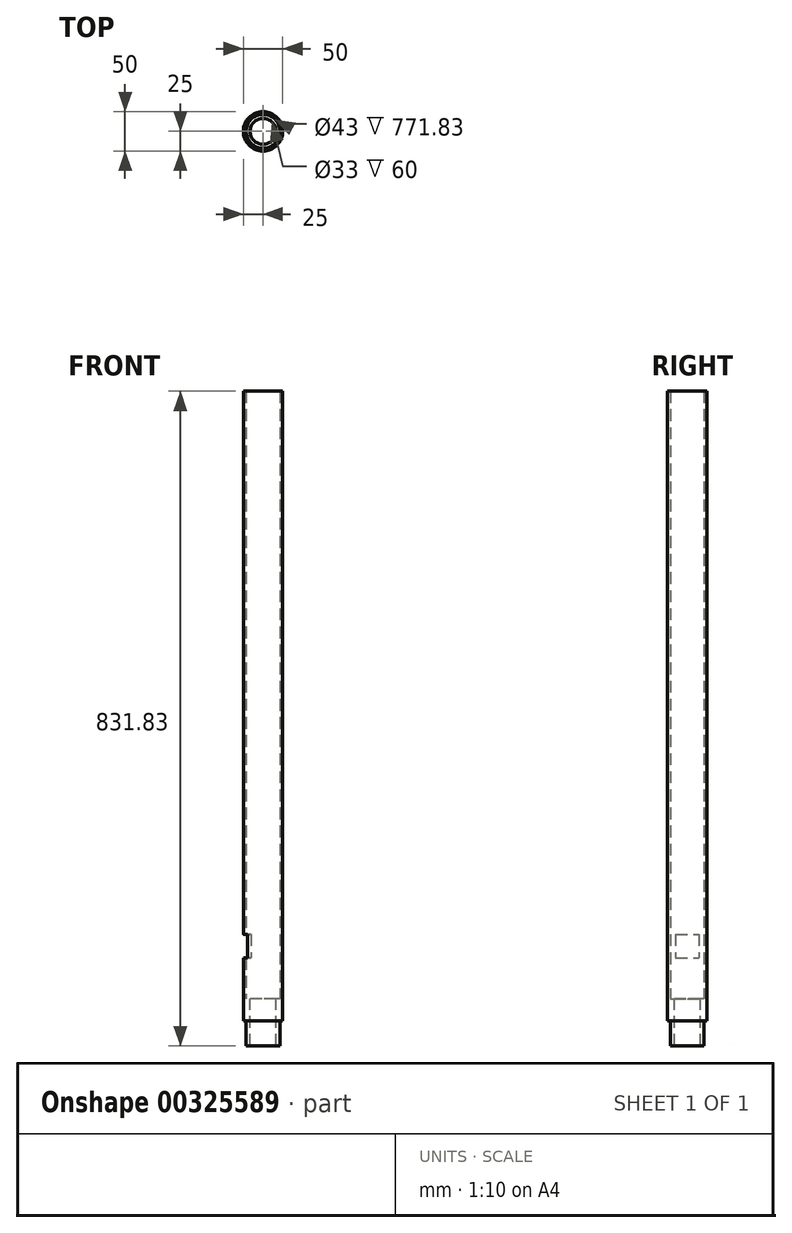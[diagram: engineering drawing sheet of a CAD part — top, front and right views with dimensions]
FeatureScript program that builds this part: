
annotation { "Feature Type Name" : "Feature", "Feature Type Description" : "" }
export const myFeature = defineFeature(function(context is Context, id is Id, definition is map)
    precondition{}
    {
        {
            var Q0;
            Q0=qCreatedBy(makeId("Top.planeOp"),FACE);
            var sketch = newSketch(context, id + "F0", { "sketchPlane" : qUnion([Q0])});
            skCircle(sketch, "E0", {"center": v(0, 0) * mm, "radius": 25 * mm});
            skCircle(sketch, "E1", {"center": v(0, 0) * mm, "radius": 21.5 * mm});
            skSolve(sketch);
        }
        {
            var Q0;
            Q0=makeQuery(id+"F0.imprint","IMPRINT",FACE,{"disambiguationData":[TD([[makeQuery(id+"F0.imprint","IMPRINT",EDGE,{"derivedFrom":sQuery(id+"F0.wireOp",EDGE,"E0")}),1.0]])]});
            extrude(context, id + "F1", {"entities" : qUnion([Q0]), "depth" : 800 * mm});
        }
        {
            var Q0;
            Q0 = qSketchRegion(id + "F0", true);
            extrude(context, id + "F2", {"entities" : qUnion([Q0]), "depth" : 200 * mm});
        }
        {
            var Q0;
            Q0=qCreatedBy(makeId("Right.planeOp"),FACE);
            var sketch = newSketch(context, id + "F3", { "sketchPlane" : qUnion([Q0])});
            skLineSegment(sketch, "E2.bottom", {"start": v(-15, 80) * mm, "end": v(15, 80) * mm});
            skLineSegment(sketch, "E2.top", {"start": v(-15, 110) * mm, "end": v(15, 110) * mm});
            skLineSegment(sketch, "E2.left", {"start": v(-15, 80) * mm, "end": v(-15, 110) * mm});
            skLineSegment(sketch, "E2.right", {"start": v(15, 80) * mm, "end": v(15, 110) * mm});
            skPoint(sketch, "E2.middle", {"position": v(0, 95) * mm});
            skSolve(sketch);
        }
        {
            var Q0;
            Q0 = qSketchRegion(id + "F3", true);
            extrude(context, id + "F4", {"entities" : qUnion([Q0]), "operationType" : NewBodyOperationType.REMOVE, "endBound" : BoundingType.THROUGH_ALL, "oppositeDirection" : true, "depth" : 25 * mm});
        }
        {
            var Q0;
            Q0=qCreatedBy(makeId("Front.planeOp"),FACE);
            var sketch = newSketch(context, id + "F5", { "sketchPlane" : qUnion([Q0])});
            skLineSegment(sketch, "E3", {"start": v(-16.5, 0) * mm, "end": v(-16.5, 28.17) * mm});
            skLineSegment(sketch, "E4", {"start": v(-16.5, 28.17) * mm, "end": v(-21.5, 28.17) * mm});
            skLineSegment(sketch, "E5", {"start": v(-21.5, 28.17) * mm, "end": v(-21.5, -31.83) * mm});
            skLineSegment(sketch, "E6", {"start": v(-21.5, -31.83) * mm, "end": v(-16.5, -31.83) * mm});
            skLineSegment(sketch, "E7", {"start": v(-16.5, -31.83) * mm, "end": v(-16.5, 0) * mm});
            skLineSegment(sketch, "E8", {"start": v(0, 23) * mm, "end": v(0, -23.62) * mm});
            skSolve(sketch);
        }
        {
            var Q0;
            Q0=makeQuery(id+"F5.imprint","IMPRINT",FACE,{"disambiguationData":[TD([[makeQuery(id+"F5.imprint","IMPRINT",EDGE,{"derivedFrom":sQuery(id+"F5.wireOp",EDGE,"E3")}),1.0]])]});
            var Q1;
            Q1=sQuery(id+"F5.wireOp",EDGE,"E5");
            var Q2;
            Q2=sQuery(id+"F5.wireOp",EDGE,"E7");
            var Q3;
            Q3=sQuery(id+"F5.wireOp",EDGE,"E6");
            var Q4;
            Q4=sQuery(id+"F5.wireOp",EDGE,"E3");
            var Q5;
            Q5=sQuery(id+"F5.wireOp",EDGE,"E4");
            var Q6;
            Q6=sQuery(id+"F5.wireOp",EDGE,"E8");
            revolve(context, id + "F6", {"operationType" : NewBodyOperationType.ADD, "entities" : qUnion([Q0]), "surfaceEntities" : qUnion([Q1, Q2, Q3, Q4, Q5]), "axis" : qUnion([Q6]), "revolveType" : RevolveType.FULL});
        }
    });
